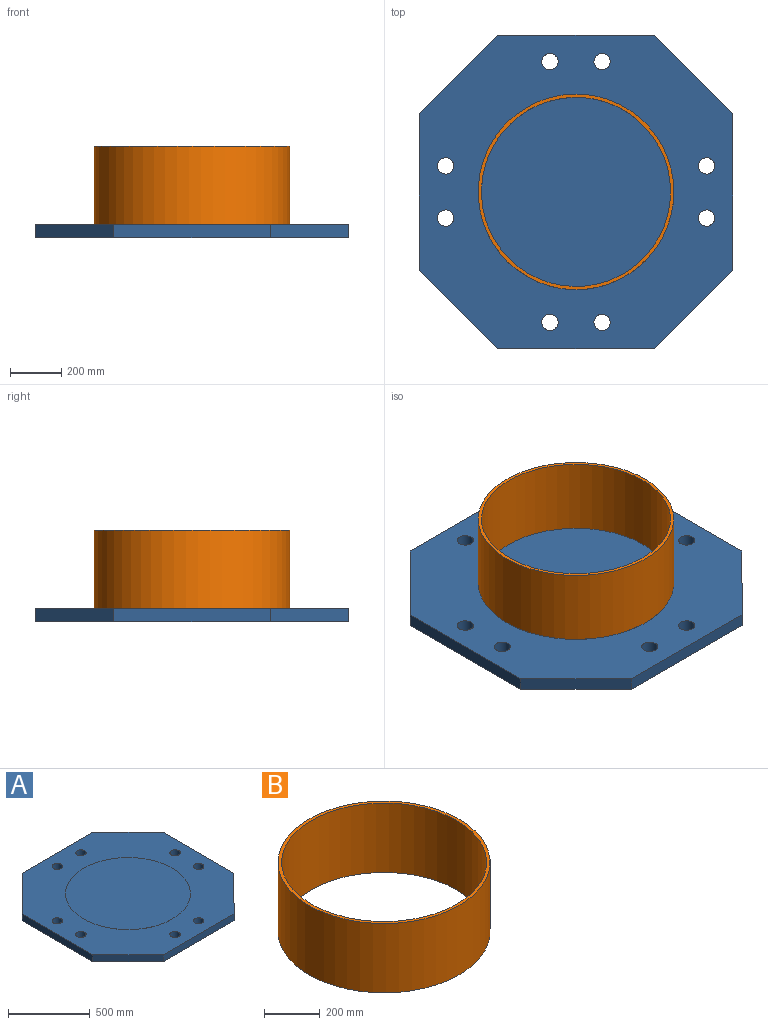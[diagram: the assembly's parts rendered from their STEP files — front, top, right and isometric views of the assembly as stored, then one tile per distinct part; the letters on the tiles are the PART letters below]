
ASSEMBLY  parts=2 mates=1
PART A: 20 faces, bbox 1219.2x1219.2x51.1 mm
  f0: plane 609.6x50.8mm, normal (0,1,0), area 30967.7mm2, adj f1,f14,f16,f17
  f1: plane 304.8x304.8mm, normal (-0.71,0.71,0), area 21897.5mm2, adj f0,f2,f16,f17
  f2: plane 609.6x50.8mm, normal (-1,0,0), area 30967.7mm2, adj f1,f3,f16,f17
  f3: plane 304.8x304.8mm, normal (-0.71,-0.71,0), area 21897.5mm2, adj f2,f4,f16,f17
  f4: plane 609.6x50.8mm, normal (0,-1,0), area 30967.7mm2, adj f3,f5,f16,f17
  f5: plane 304.8x304.8mm, normal (0.71,-0.71,0), area 21897.5mm2, adj f4,f6,f16,f17
  f6: plane 609.6x50.8mm, normal (1,0,0), area 30967.7mm2, adj f5,f14,f16,f17
  f7: cylinder r=31.75mm len=63.5mm, axis (0,0,1), area 10134.1mm2, adj f16,f17
  f8: cylinder r=31.75mm len=63.5mm, axis (0,0,1), area 10134.1mm2, adj f16,f17
  f9: cylinder r=31.75mm len=63.5mm, axis (0,0,1), area 10134.1mm2, adj f16,f17
  f10: cylinder r=31.75mm len=63.5mm, axis (0,0,1), area 10134.1mm2, adj f16,f17
  f11: cylinder r=31.75mm len=63.5mm, axis (0,0,1), area 10134.1mm2, adj f16,f17
  f12: cylinder r=31.75mm len=63.5mm, axis (0,0,1), area 10134.1mm2, adj f16,f17
  f13: cylinder r=31.75mm len=63.5mm, axis (0,0,1), area 10134.1mm2, adj f16,f17
  f14: plane 304.8x304.8mm, normal (0.71,0.71,0), area 21897.5mm2, adj f0,f6,f16,f17
  f15: cylinder r=31.75mm len=63.5mm, axis (0,0,1), area 10134.1mm2, adj f16,f17
  f16: plane 1219.2x1219.2mm, normal (0,0,-1), area 1275307.2mm2, adj f0,f1,f2,f3,f4,f5,f6,f7
  f17: plane 1219.2x1219.2mm, normal (0,0,1), area 819270.5mm2, adj f0,f1,f2,f3,f4,f5,f6,f7
  f18: cylinder r=381mm len=762mm, axis (0,0,-1), area 608mm2, adj f17,f19
  f19: plane 762x762mm, normal (0,0,1), area 456036.7mm2, adj f18
PART B: 4 faces, bbox 762x762x304.8 mm
  f0: cylinder r=368.3mm len=736.6mm, axis (0,0,-1), area 705336.8mm2, adj f2,f3
  f1: cylinder r=381mm len=762mm, axis (0,0,-1), area 729658.8mm2, adj f2,f3
  f2: plane 762x762mm, normal (0,0,1), area 29895.7mm2, adj f0,f1
  f3: plane 762x762mm, normal (0,0,-1), area 29895.7mm2, adj f0,f1
PLACE A t=(2906.22,-447.98,-154.62)mm
PLACE B t=(1120.98,-464.22,-154.37)mm
MATE fastened B.f0 <-> A.f18  axis (0,0,-1) through (-297.1,-1057.58,-154.37)mm
